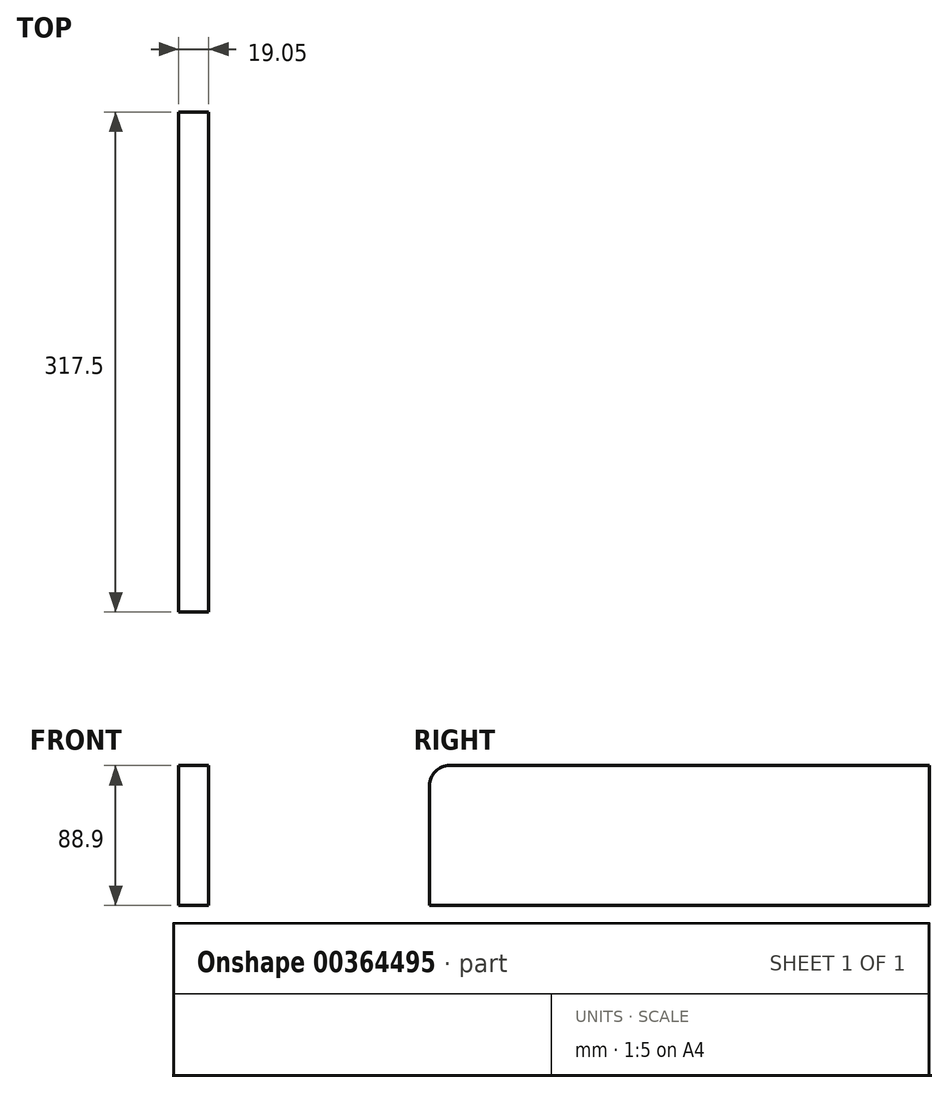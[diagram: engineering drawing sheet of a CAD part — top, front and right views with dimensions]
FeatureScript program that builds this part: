
annotation { "Feature Type Name" : "Feature", "Feature Type Description" : "" }
export const myFeature = defineFeature(function(context is Context, id is Id, definition is map)
    precondition{}
    {
        {
            var Q0;
            Q0=qCreatedBy(makeId("Right.planeOp"),FACE);
            var sketch = newSketch(context, id + "F0", { "sketchPlane" : qUnion([Q0])});
            skLineSegment(sketch, "E0.bottom", {"start": v(0, 0) * mm, "end": v(317.5, 0) * mm});
            skLineSegment(sketch, "E0.top", {"start": v(12.7, 88.9) * mm, "end": v(317.5, 88.9) * mm});
            skLineSegment(sketch, "E0.left", {"start": v(0, 0) * mm, "end": v(0, 76.2) * mm});
            skLineSegment(sketch, "E0.right", {"start": v(317.5, 0) * mm, "end": v(317.5, 88.9) * mm});
            skPoint(sketch, "E1.visualSharp", {"position": v(0, 88.9) * mm});
            skArc(sketch, "E1.filletArc", {"start": v(12.7, 88.9) * mm, "mid": v(3.72, 85.18) * mm, "end": v(0, 76.2) * mm});
            skSolve(sketch);
        }
        {
            var Q0;
            Q0=makeQuery(id+"F0.imprint","IMPRINT",FACE,{"disambiguationData":[TD([[makeQuery(id+"F0.imprint","IMPRINT",EDGE,{"derivedFrom":sQuery(id+"F0.wireOp",EDGE,"E0.bottom")}),1.0]])]});
            extrude(context, id + "F1", {"entities" : qUnion([Q0]), "depth" : 19.05 * mm});
        }
    });
